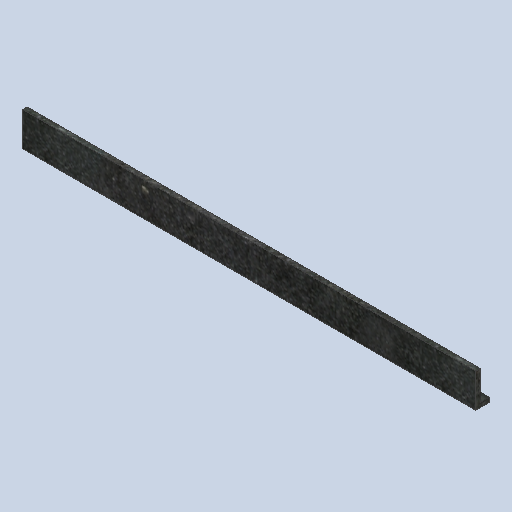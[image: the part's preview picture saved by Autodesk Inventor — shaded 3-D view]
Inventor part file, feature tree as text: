
AUTODESK INVENTOR PART (.ipt)
format: ipt  version: 2024.3 (Build 283343000, 343)  size: 237,056 bytes
history: native  units: mm
features: extrude x1, sketch x1
ambient origin geometry x8: Origin, YZ Plane, XZ Plane, XY Plane, X Axis, Y Axis, Z Axis, Center Point
bodies: Solid1 (feature_tree)
feature tree (2):
  extrude  "Extrusion1"  Depth=2.0mm
  sketch  "Sketch1"  dims[d0=15.0mm d1=2.0mm d2=2.0mm d3=6.0mm d4=200.0mm d5=0.0mm]
